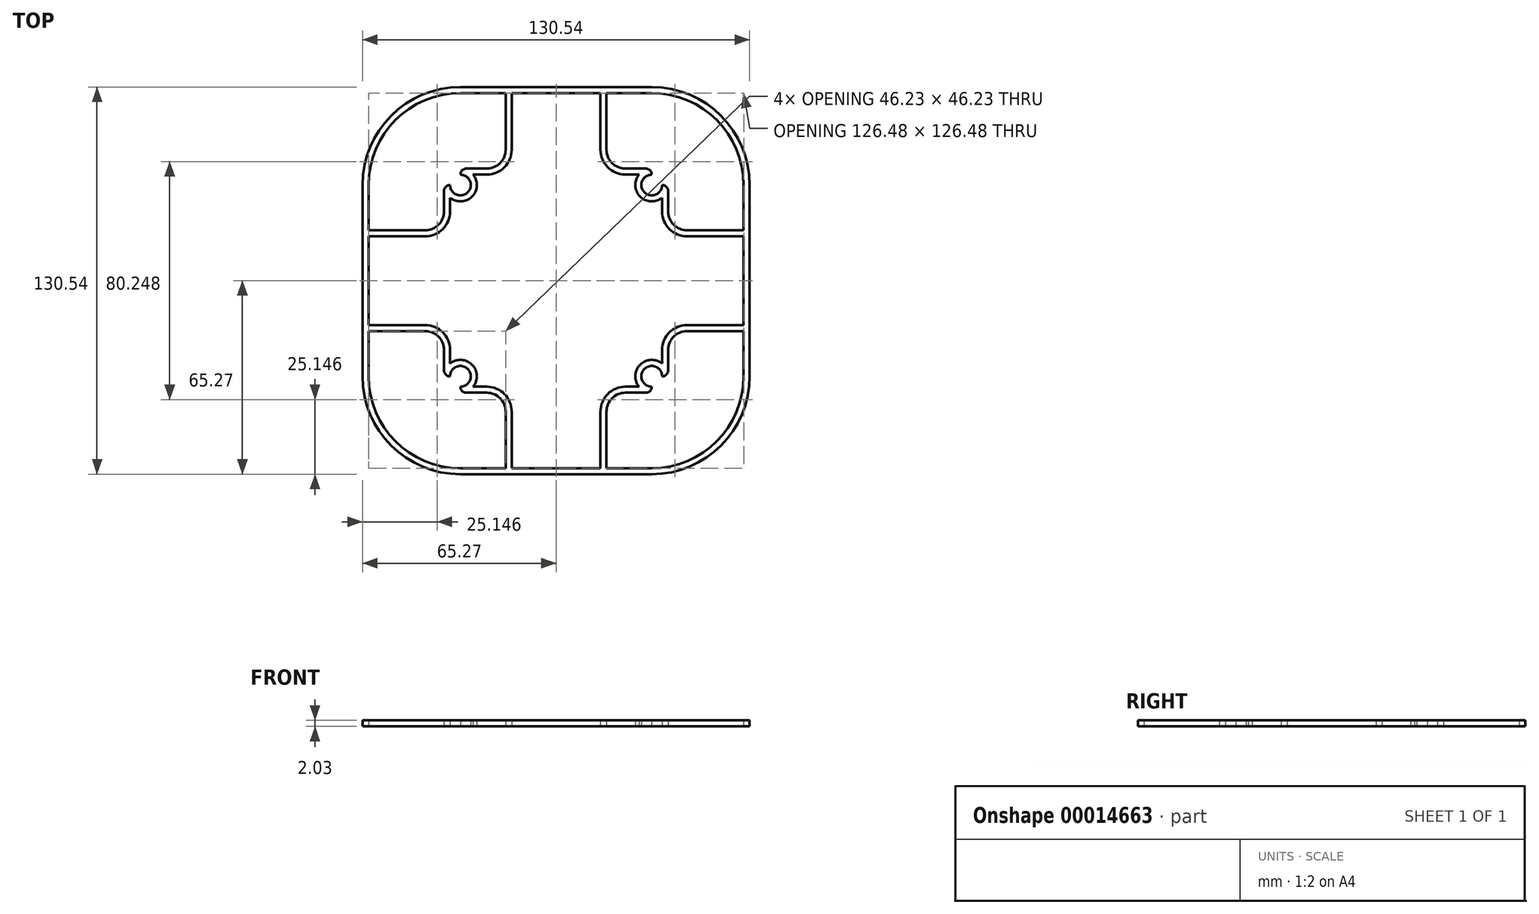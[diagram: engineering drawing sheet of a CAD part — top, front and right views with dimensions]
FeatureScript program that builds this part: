
annotation { "Feature Type Name" : "Feature", "Feature Type Description" : "" }
export const myFeature = defineFeature(function(context is Context, id is Id, definition is map)
    precondition{}
    {
        {
            var Q0;
            Q0=qCreatedBy(makeId("Top.planeOp"),FACE);
            var sketch = newSketch(context, id + "F0", { "sketchPlane" : qUnion([Q0])});
            skLineSegment(sketch, "E0.rect.bottom", {"start": v(-35.75, 35.75) * mm, "end": v(35.75, 35.75) * mm, "construction": true});
            skLineSegment(sketch, "E0.rect.top", {"start": v(-35.75, -35.75) * mm, "end": v(35.75, -35.75) * mm, "construction": true});
            skLineSegment(sketch, "E0.rect.left", {"start": v(-35.75, 35.75) * mm, "end": v(-35.75, -35.75) * mm, "construction": true});
            skLineSegment(sketch, "E0.rect.right", {"start": v(35.75, 35.75) * mm, "end": v(35.75, -35.75) * mm, "construction": true});
            skPoint(sketch, "E0.rect.middle", {"position": v(0, 0) * mm});
            skCircle(sketch, "E1", {"center": v(-32.25, 32.25) * mm, "radius": 3.5 * mm, "construction": true});
            skLineSegment(sketch, "E2.rect.bottom", {"start": v(-32.25, 32.25) * mm, "end": v(32.25, 32.25) * mm, "construction": true});
            skLineSegment(sketch, "E2.rect.top", {"start": v(-32.25, -32.25) * mm, "end": v(32.25, -32.25) * mm, "construction": true});
            skLineSegment(sketch, "E2.rect.left", {"start": v(-32.25, 32.25) * mm, "end": v(-32.25, -32.25) * mm, "construction": true});
            skLineSegment(sketch, "E2.rect.right", {"start": v(32.25, 32.25) * mm, "end": v(32.25, -32.25) * mm, "construction": true});
            skCircle(sketch, "E3", {"center": v(-32.25, 32.25) * mm, "radius": 27.5 * mm, "construction": true});
            skLineSegment(sketch, "E4.rect.bottom", {"start": v(-32.25, 65.27) * mm, "end": v(32.25, 65.27) * mm});
            skLineSegment(sketch, "E4.rect.top", {"start": v(-32.25, -65.27) * mm, "end": v(32.25, -65.27) * mm});
            skLineSegment(sketch, "E4.rect.left", {"start": v(-65.27, 32.25) * mm, "end": v(-65.27, -32.25) * mm});
            skLineSegment(sketch, "E4.rect.right", {"start": v(65.27, 32.25) * mm, "end": v(65.27, -32.25) * mm});
            skPoint(sketch, "E5.visualSharp", {"position": v(-65.27, 65.27) * mm});
            skArc(sketch, "E6.filletArc", {"start": v(-32.25, 65.27) * mm, "mid": v(-55.6, 55.6) * mm, "end": v(-65.27, 32.25) * mm});
            skPoint(sketch, "E7.visualSharp", {"position": v(65.27, 65.27) * mm});
            skArc(sketch, "E7.filletArc", {"start": v(65.27, 32.25) * mm, "mid": v(55.6, 55.6) * mm, "end": v(32.25, 65.27) * mm});
            skPoint(sketch, "E8.visualSharp", {"position": v(65.27, -65.27) * mm});
            skArc(sketch, "E8.filletArc", {"start": v(32.25, -65.27) * mm, "mid": v(55.6, -55.6) * mm, "end": v(65.27, -32.25) * mm});
            skPoint(sketch, "E9.visualSharp", {"position": v(-65.27, -65.27) * mm});
            skArc(sketch, "E9.filletArc", {"start": v(-65.27, -32.25) * mm, "mid": v(-55.6, -55.6) * mm, "end": v(-32.25, -65.27) * mm});
            skCircle(sketch, "E10", {"center": v(32.25, 32.25) * mm, "radius": 27.5 * mm, "construction": true});
            skCircle(sketch, "E11", {"center": v(-32.25, -32.25) * mm, "radius": 27.5 * mm, "construction": true});
            skCircle(sketch, "E12", {"center": v(32.25, -32.25) * mm, "radius": 27.5 * mm, "construction": true});
            skCircle(sketch, "E13", {"center": v(32.25, 32.25) * mm, "radius": 3.5 * mm, "construction": true});
            skCircle(sketch, "E14", {"center": v(32.25, -32.25) * mm, "radius": 3.5 * mm, "construction": true});
            skCircle(sketch, "E15", {"center": v(-32.25, -32.25) * mm, "radius": 3.5 * mm, "construction": true});
            skArc(sketch, "E16.0", {"start": v(-32.25, 63.24) * mm, "mid": v(-54.16, 54.16) * mm, "end": v(-63.24, 32.25) * mm});
            skLineSegment(sketch, "E16.1", {"start": v(-63.24, 32.25) * mm, "end": v(-63.24, -32.25) * mm});
            skArc(sketch, "E16.2", {"start": v(-63.24, -32.25) * mm, "mid": v(-54.16, -54.16) * mm, "end": v(-32.25, -63.24) * mm});
            skLineSegment(sketch, "E16.3", {"start": v(-32.25, -63.24) * mm, "end": v(32.25, -63.24) * mm});
            skArc(sketch, "E16.4", {"start": v(32.25, -63.24) * mm, "mid": v(54.16, -54.16) * mm, "end": v(63.24, -32.25) * mm});
            skLineSegment(sketch, "E16.5", {"start": v(-32.25, 63.24) * mm, "end": v(32.25, 63.24) * mm});
            skLineSegment(sketch, "E16.6", {"start": v(63.24, 32.25) * mm, "end": v(63.24, -32.25) * mm});
            skArc(sketch, "E16.7", {"start": v(63.24, 32.25) * mm, "mid": v(54.16, 54.16) * mm, "end": v(32.25, 63.24) * mm});
            skLineSegment(sketch, "E17", {"start": v(-32.25, 32.25) * mm, "end": v(-59.75, 32.25) * mm, "construction": true});
            skLineSegment(sketch, "E18", {"start": v(-59.75, 32.25) * mm, "end": v(-56.07, 46) * mm, "construction": true});
            skLineSegment(sketch, "E19", {"start": v(-56.07, 46) * mm, "end": v(-32.25, 32.25) * mm, "construction": true});
            skSolve(sketch);
        }
        {
            var Q0;
            Q0=makeQuery(id+"F0.imprint","IMPRINT",FACE,{"disambiguationData":[TD([[makeQuery(id+"F0.imprint","IMPRINT",EDGE,{"derivedFrom":sQuery(id+"F0.wireOp",EDGE,"E4.rect.bottom")}),-1.0]])]});
            extrude(context, id + "F1", {"entities" : qUnion([Q0]), "depth" : 2.03 * mm});
        }
        {
            var Q0;
            Q0=qCreatedBy(makeId("Top.planeOp"),FACE);
            var sketch = newSketch(context, id + "F2", { "sketchPlane" : qUnion([Q0])});
            skArc(sketch, "E20", {"start": v(-35.75, 32.25) * mm, "mid": v(-29.78, 29.78) * mm, "end": v(-32.25, 35.75) * mm});
            skLineSegment(sketch, "E21", {"start": v(-32.25, 35.75) * mm, "end": v(-32.25, 37.78) * mm});
            skLineSegment(sketch, "E22", {"start": v(-35.75, 32.25) * mm, "end": v(-37.78, 32.25) * mm});
            skArc(sketch, "E23.0", {"start": v(-35.75, 27.97) * mm, "mid": v(-28.34, 28.34) * mm, "end": v(-27.97, 35.75) * mm});
            skLineSegment(sketch, "E24", {"start": v(-37.78, 32.25) * mm, "end": v(-37.78, 23.36) * mm});
            skLineSegment(sketch, "E25", {"start": v(-44.13, 17.01) * mm, "end": v(-63.24, 17.01) * mm});
            skLineSegment(sketch, "E26", {"start": v(-63.24, 17.01) * mm, "end": v(-63.24, 14.98) * mm});
            skLineSegment(sketch, "E27", {"start": v(-63.24, 14.98) * mm, "end": v(-44.13, 14.98) * mm});
            skLineSegment(sketch, "E28", {"start": v(-35.75, 23.36) * mm, "end": v(-35.75, 27.97) * mm});
            skLineSegment(sketch, "E29", {"start": v(-27.97, 35.75) * mm, "end": v(-23.36, 35.75) * mm});
            skLineSegment(sketch, "E30", {"start": v(-14.98, 44.13) * mm, "end": v(-14.98, 63.24) * mm});
            skLineSegment(sketch, "E31", {"start": v(-14.98, 63.24) * mm, "end": v(-17.01, 63.24) * mm});
            skLineSegment(sketch, "E32", {"start": v(-17.01, 63.24) * mm, "end": v(-17.01, 44.13) * mm});
            skLineSegment(sketch, "E33", {"start": v(-23.36, 37.78) * mm, "end": v(-32.25, 37.78) * mm});
            skPoint(sketch, "E34.visualSharp", {"position": v(-17.01, 37.78) * mm});
            skArc(sketch, "E34.filletArc", {"start": v(-23.36, 37.78) * mm, "mid": v(-18.87, 39.64) * mm, "end": v(-17.01, 44.13) * mm});
            skPoint(sketch, "E35.visualSharp", {"position": v(-37.78, 17.01) * mm});
            skArc(sketch, "E35.filletArc", {"start": v(-44.13, 17.01) * mm, "mid": v(-39.64, 18.87) * mm, "end": v(-37.78, 23.36) * mm});
            skPoint(sketch, "E36.visualSharp", {"position": v(-14.98, 35.75) * mm});
            skArc(sketch, "E36.filletArc", {"start": v(-23.36, 35.75) * mm, "mid": v(-17.43, 38.2) * mm, "end": v(-14.98, 44.13) * mm});
            skPoint(sketch, "E37.visualSharp", {"position": v(-35.75, 14.98) * mm});
            skArc(sketch, "E37.filletArc", {"start": v(-44.13, 14.98) * mm, "mid": v(-38.2, 17.43) * mm, "end": v(-35.75, 23.36) * mm});
            skSolve(sketch);
        }
        {
            var Q0;
            Q0=makeQuery(id+"F2.imprint","IMPRINT",FACE,{"disambiguationData":[TD([[makeQuery(id+"F2.imprint","IMPRINT",EDGE,{"derivedFrom":sQuery(id+"F2.wireOp",EDGE,"E20")}),-1.0]])]});
            extrude(context, id + "F3", {"entities" : qUnion([Q0]), "depth" : 2.03 * mm});
        }
        {
            var Q0;
            Q0=makeQuery(id+"F3.opExtrude","SWEPT_EDGE",EDGE,{"disambiguationData":[OSD([sQuery(id+"F2.wireOp",EDGE,"E21"),sQuery(id+"F2.wireOp",EDGE,"E33")])]});
            var Q1;
            Q1=makeQuery(id+"F3.opExtrude","SWEPT_EDGE",EDGE,{"disambiguationData":[OSD([sQuery(id+"F2.wireOp",EDGE,"E22"),sQuery(id+"F2.wireOp",EDGE,"E24")])]});
            fillet(context, id + "F4", {"entities" : qUnion([Q0, Q1]), "radius" : 2.03 * mm, "tangentPropagation" : true, "allowEdgeOverflow" : false});
        }
        {
            var Q0;
            Q0=makeQuery(id+"F3.opExtrude","SWEPT_BODY",BODY,{"disambiguationData":[OSD([sQuery(id+"F2.wireOp",EDGE,"E20"),sQuery(id+"F2.wireOp",EDGE,"E21"),sQuery(id+"F2.wireOp",EDGE,"E22"),sQuery(id+"F2.wireOp",EDGE,"E23.0"),sQuery(id+"F2.wireOp",EDGE,"E24"),sQuery(id+"F2.wireOp",EDGE,"E25"),sQuery(id+"F2.wireOp",EDGE,"E26"),sQuery(id+"F2.wireOp",EDGE,"E27"),sQuery(id+"F2.wireOp",EDGE,"E28"),sQuery(id+"F2.wireOp",EDGE,"E29"),sQuery(id+"F2.wireOp",EDGE,"E30"),sQuery(id+"F2.wireOp",EDGE,"E31"),sQuery(id+"F2.wireOp",EDGE,"E32"),sQuery(id+"F2.wireOp",EDGE,"E33"),sQuery(id+"F2.wireOp",EDGE,"E34.filletArc"),sQuery(id+"F2.wireOp",EDGE,"E35.filletArc"),sQuery(id+"F2.wireOp",EDGE,"E36.filletArc"),sQuery(id+"F2.wireOp",EDGE,"E37.filletArc")])]});
            var Q1;
            Q1=qCreatedBy(makeId("Right.planeOp"),FACE);
            mirror(context, id + "F5", {"entities" : qUnion([Q0]), "mirrorPlane" : qUnion([Q1])});
        }
        {
            var Q0;
            Q0=makeQuery(id+"F3.opExtrude","SWEPT_BODY",BODY,{"disambiguationData":[OSD([sQuery(id+"F2.wireOp",EDGE,"E20"),sQuery(id+"F2.wireOp",EDGE,"E21"),sQuery(id+"F2.wireOp",EDGE,"E22"),sQuery(id+"F2.wireOp",EDGE,"E23.0"),sQuery(id+"F2.wireOp",EDGE,"E24"),sQuery(id+"F2.wireOp",EDGE,"E25"),sQuery(id+"F2.wireOp",EDGE,"E26"),sQuery(id+"F2.wireOp",EDGE,"E27"),sQuery(id+"F2.wireOp",EDGE,"E28"),sQuery(id+"F2.wireOp",EDGE,"E29"),sQuery(id+"F2.wireOp",EDGE,"E30"),sQuery(id+"F2.wireOp",EDGE,"E31"),sQuery(id+"F2.wireOp",EDGE,"E32"),sQuery(id+"F2.wireOp",EDGE,"E33"),sQuery(id+"F2.wireOp",EDGE,"E34.filletArc"),sQuery(id+"F2.wireOp",EDGE,"E35.filletArc"),sQuery(id+"F2.wireOp",EDGE,"E36.filletArc"),sQuery(id+"F2.wireOp",EDGE,"E37.filletArc")])]});
            var Q1;
            Q1=makeQuery(id+"F5.opPattern","COPY",BODY,{"derivedFrom":makeQuery(id+"F3.opExtrude","SWEPT_BODY",BODY,{"disambiguationData":[OSD([sQuery(id+"F2.wireOp",EDGE,"E20"),sQuery(id+"F2.wireOp",EDGE,"E21"),sQuery(id+"F2.wireOp",EDGE,"E22"),sQuery(id+"F2.wireOp",EDGE,"E23.0"),sQuery(id+"F2.wireOp",EDGE,"E24"),sQuery(id+"F2.wireOp",EDGE,"E25"),sQuery(id+"F2.wireOp",EDGE,"E26"),sQuery(id+"F2.wireOp",EDGE,"E27"),sQuery(id+"F2.wireOp",EDGE,"E28"),sQuery(id+"F2.wireOp",EDGE,"E29"),sQuery(id+"F2.wireOp",EDGE,"E30"),sQuery(id+"F2.wireOp",EDGE,"E31"),sQuery(id+"F2.wireOp",EDGE,"E32"),sQuery(id+"F2.wireOp",EDGE,"E33"),sQuery(id+"F2.wireOp",EDGE,"E34.filletArc"),sQuery(id+"F2.wireOp",EDGE,"E35.filletArc"),sQuery(id+"F2.wireOp",EDGE,"E36.filletArc"),sQuery(id+"F2.wireOp",EDGE,"E37.filletArc")])]}),"instanceName":"1"});
            var Q2;
            Q2=qCreatedBy(makeId("Front.planeOp"),FACE);
            mirror(context, id + "F6", {"operationType" : NewBodyOperationType.ADD, "entities" : qUnion([Q0, Q1]), "mirrorPlane" : qUnion([Q2])});
        }
    });
